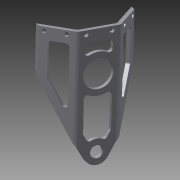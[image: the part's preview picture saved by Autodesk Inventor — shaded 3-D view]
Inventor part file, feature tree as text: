
AUTODESK INVENTOR PART (.ipt)
format: ipt  version: 2012 (Build 160160000, 160)  size: 297,984 bytes
history: native  units: in
note: dims shown in document units (in); Inventor stores cm internally (conversion verified against a paired STEP export)
features: sketch x6, other x4, projected_geometry x4, sheet_metal_op x3, fillet x1
ambient origin geometry x8: Origin, YZ Plane, XZ Plane, XY Plane, X Axis, Y Axis, Z Axis, Center Point
bodies: Solid1 (feature_tree)
feature tree (18):
  sheet_metal_op  "Face1"
  fillet  "Fillet1"  Radius=1.1796in
  sheet_metal_op  "Fold1"
  sheet_metal_op  "Fold2"
  sketch  "Sketch1"  dims[d2=1.289in]
  other  "Plate1"
  sketch  "Sketch3"  dims[d3=0.875in]
  sketch  "Sketch4"  dims[d4=0.5898in]
  sketch  "Sketch5"  dims[d5=3.5in]
  projected_geometry  "Projected Loop1"
  projected_geometry  "Projected Loop2"
  projected_geometry  "Projected Loop3"
  projected_geometry  "Projected Loop4"
  sketch  "Sketch6"  dims[d6=0.375in]
  sketch  "Sketch7"  dims[d7=0.375in d9=0.1875in d10=0.1875in d11=0.625in d12=0.625in d13=0.1875in d14=0.375in d15=0.1875in d16=0.3125in d17=0.3125in d18=0.125in d29=0.375in d30=0.375in d31=0.375in d32=0.375in d33=0.375in d34=0.375in d39=0.0938in d40=0.1875in d41=0.125in d42=0.0625in d43=0.25in d44=0.125in d45=45.0deg d46=0.0625in d47=1.1593in d48=1.1593in d49=0.125in d50=0.0625in d51=0.25in d52=0.125in d53=45.0deg d54=0.0625in d59=1.5in d60=0.0in d61=0.14in d62=0.75in d63=0.2148in d64=0.2148in d65=0.125in d66=0.25in d68=0.625in d69=0.14in d70=0.125in d71=0.125in d72=0.0in d73=0.14in d74=0.125in d75=0.625in d76=0.25in d77=0.125in d78=0.0in d83=0.375in d84=0.25in d85=0.25in]
  other  "Cut2"
  other  "Cut3"
  other  "Cut4"
